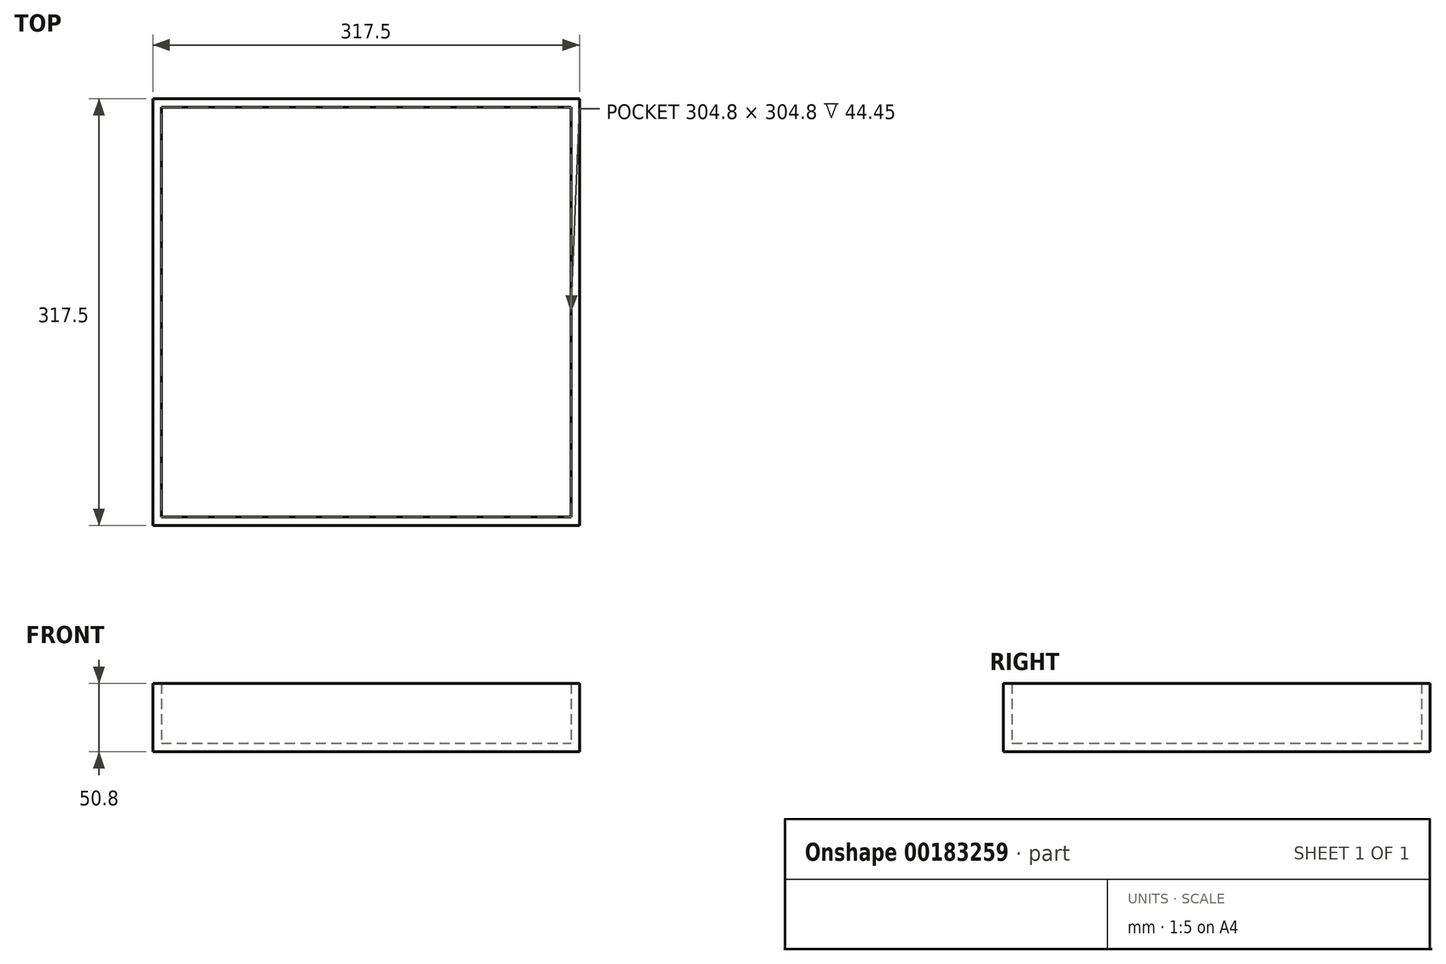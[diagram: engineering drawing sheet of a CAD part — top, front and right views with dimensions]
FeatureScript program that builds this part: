
annotation { "Feature Type Name" : "Feature", "Feature Type Description" : "" }
export const myFeature = defineFeature(function(context is Context, id is Id, definition is map)
    precondition{}
    {
        {
            var Q0;
            Q0=qCreatedBy(makeId("Top.planeOp"),FACE);
            var sketch = newSketch(context, id + "F0", { "sketchPlane" : qUnion([Q0])});
            skLineSegment(sketch, "E0.bottom", {"start": v(0, 0) * mm, "end": v(317.5, 0) * mm});
            skLineSegment(sketch, "E0.top", {"start": v(0, 317.5) * mm, "end": v(317.5, 317.5) * mm});
            skLineSegment(sketch, "E0.left", {"start": v(0, 0) * mm, "end": v(0, 317.5) * mm});
            skLineSegment(sketch, "E0.right", {"start": v(317.5, 0) * mm, "end": v(317.5, 317.5) * mm});
            skLineSegment(sketch, "E1.bottom", {"start": v(6.35, 6.35) * mm, "end": v(311.15, 6.35) * mm});
            skLineSegment(sketch, "E1.top", {"start": v(6.35, 311.15) * mm, "end": v(311.15, 311.15) * mm});
            skLineSegment(sketch, "E1.left", {"start": v(6.35, 6.35) * mm, "end": v(6.35, 311.15) * mm});
            skLineSegment(sketch, "E1.right", {"start": v(311.15, 6.35) * mm, "end": v(311.15, 311.15) * mm});
            skSolve(sketch);
        }
        {
            var Q0;
            Q0=makeQuery(id+"F0.imprint","IMPRINT",FACE,{"disambiguationData":[TD([[makeQuery(id+"F0.imprint","IMPRINT",EDGE,{"derivedFrom":sQuery(id+"F0.wireOp",EDGE,"E0.bottom")}),1.0]])]});
            extrude(context, id + "F1", {"entities" : qUnion([Q0]), "depth" : 50.8 * mm});
        }
        {
            var Q0;
            Q0=qCreatedBy(makeId("Top.planeOp"),FACE);
            var sketch = newSketch(context, id + "F2", { "sketchPlane" : qUnion([Q0])});
            skLineSegment(sketch, "E2.bottom", {"start": v(0, 0) * mm, "end": v(317.5, 0) * mm});
            skLineSegment(sketch, "E2.top", {"start": v(0, 317.5) * mm, "end": v(317.5, 317.5) * mm});
            skLineSegment(sketch, "E2.left", {"start": v(0, 0) * mm, "end": v(0, 317.5) * mm});
            skLineSegment(sketch, "E2.right", {"start": v(317.5, 0) * mm, "end": v(317.5, 317.5) * mm});
            skSolve(sketch);
        }
        {
            var Q0;
            Q0=makeQuery(id+"F2.imprint","IMPRINT",FACE,{"disambiguationData":[TD([[makeQuery(id+"F2.imprint","IMPRINT",EDGE,{"derivedFrom":sQuery(id+"F2.wireOp",EDGE,"E2.bottom")}),1.0]])]});
            extrude(context, id + "F3", {"entities" : qUnion([Q0]), "operationType" : NewBodyOperationType.ADD, "depth" : 6.35 * mm});
        }
    });
